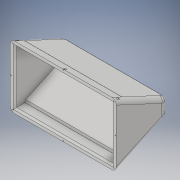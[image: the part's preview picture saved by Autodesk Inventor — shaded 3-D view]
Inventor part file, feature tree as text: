
AUTODESK INVENTOR PART (.ipt)
format: ipt  version: 2018 (Build 220112000, 112)  size: 304,128 bytes
history: native  units: in
note: dims shown in document units (in); Inventor stores cm internally (conversion verified against a paired STEP export)
features: extrude x6, sketch x6, draft x2, chamfer x2, fillet x2, plane x1
ambient origin geometry x8: Origin, YZ Plane, XZ Plane, XY Plane, X Axis, Y Axis, Z Axis, Center Point
bodies: Body1 (feature_tree)
feature tree (19):
  extrude  "Extrusion3"  Depth=7.927in
  draft  "FaceDraft1"
  draft  "FaceDraft2"
  extrude  "Extrusion4"  [1 undecoded]
  sketch  "Sketch5"  dims[d11=-0.1718in]
  chamfer  "Chamfer1"  Distance=3.5in
  sketch  "Sketch6"  dims[d12=0.35in]
  fillet  "Fillet2"  Radius=0.315in
  fillet  "Fillet3"  Radius=0.5906in
  extrude  "Extrusion9"  Depth=0.125in
  plane  "Work Plane1"
  extrude  "Extrusion10"  Depth=0.125in
  extrude  "Extrusion11"  Depth=0.125in
  extrude  "Extrusion12"  Depth=0.125in
  chamfer  "Chamfer4"  Distance=0.063in
  sketch  "Sketch1"  dims[d0=4.699in d1=7.927in]
  sketch  "Sketch3"  dims[d8=4.0in d9=0.0in d10=-0.1718in]
  sketch  "Sketch7"  dims[d13=0.35in d14=3.5in d15=0.0in]
  sketch  "Sketch8"  dims[d21=0.125in d22=0.125in d23=45.0deg d33=0.315in d34=0.5906in d35=0.0625in d36=0.088in d39=0.088in d40=0.0625in d42=0.063in d43=0.0625in d44=0.063in d45=0.0625in d47=45.0deg d48=0.0625in d49=0.088in d50=0.063in d51=0.0625in d52=45.0deg d53=0.0625in d54=0.088in d59=0.0625in d60=0.063in d61=3.0in d62=0.0in d63=-0.4in d64=0.125in d65=0.125in d66=0.125in d67=0.125in d68=0.125in d69=0.125in d70=0.35in d71=0.0in d72=0.25in d73=0.0in d74=0.0in d75=0.125in d76=0.0in d77=0.0in d78=0.0in d79=0.0in d80=0.25in d81=0.125in d82=0.0in d83=0.12in d84=0.125in d85=45.0deg]
note: 1 required parameter value undecoded (feature->parameter linkage not recoverable at this tier; creation-order binding heuristic only, values carry confidence <= 0.55)
